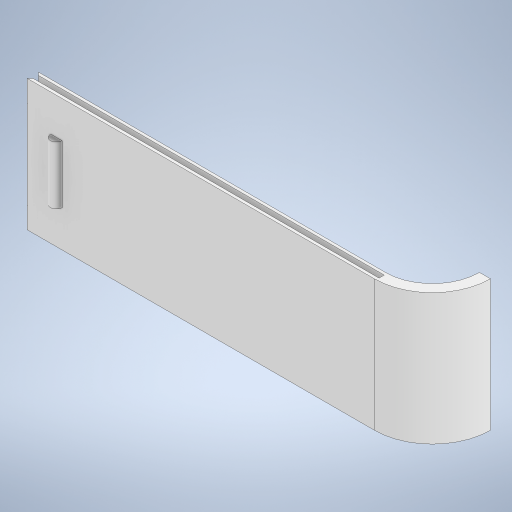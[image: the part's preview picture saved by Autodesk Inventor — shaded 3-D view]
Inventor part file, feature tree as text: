
AUTODESK INVENTOR PART (.ipt)
format: ipt  version: 2023 (Build 270158000, 158)  size: 267,776 bytes
history: native  units: mm
features: extrude x5, sketch x4, mirror x1, plane x1
ambient origin geometry x8: Origin, YZ Plane, XZ Plane, XY Plane, X Axis, Y Axis, Z Axis, Center Point
bodies: Solid1 (feature_tree)
feature tree (11):
  extrude  "Extrusion1"  Depth=69.8mm
  sketch  "Sketch3"  dims[d6=1.9mm d7=22.6mm]
  extrude  "Extrusion2"  Depth=22.6mm
  extrude  "Extrusion3"  Depth=3.2mm
  mirror  "Mirror1"
  plane  "Work Plane1"
  extrude  "Extrusion4"  Depth=60.1mm TaperAngle=0.0deg
  extrude  "Extrusion5"  Depth=0.5mm
  sketch  "Sketch1"  dims[d4=10.0mm d5=69.8mm]
  sketch  "Sketch4"  dims[d8=0.0mm d11=3.2mm]
  sketch  "Sketch5"  dims[d12=0.9mm d13=60.1mm d14=0.0mm d18=0.5mm d19=0.5mm d20=0.5mm d21=0.5mm d22=0.5mm d23=-7.853982mm d26=0.7mm d27=0.25mm d28=10.4mm d29=0.0mm d30=1.0mm d31=5.0mm d32=10.0mm d33=0.0mm d24=0.5mm d25=0.872665mm]
